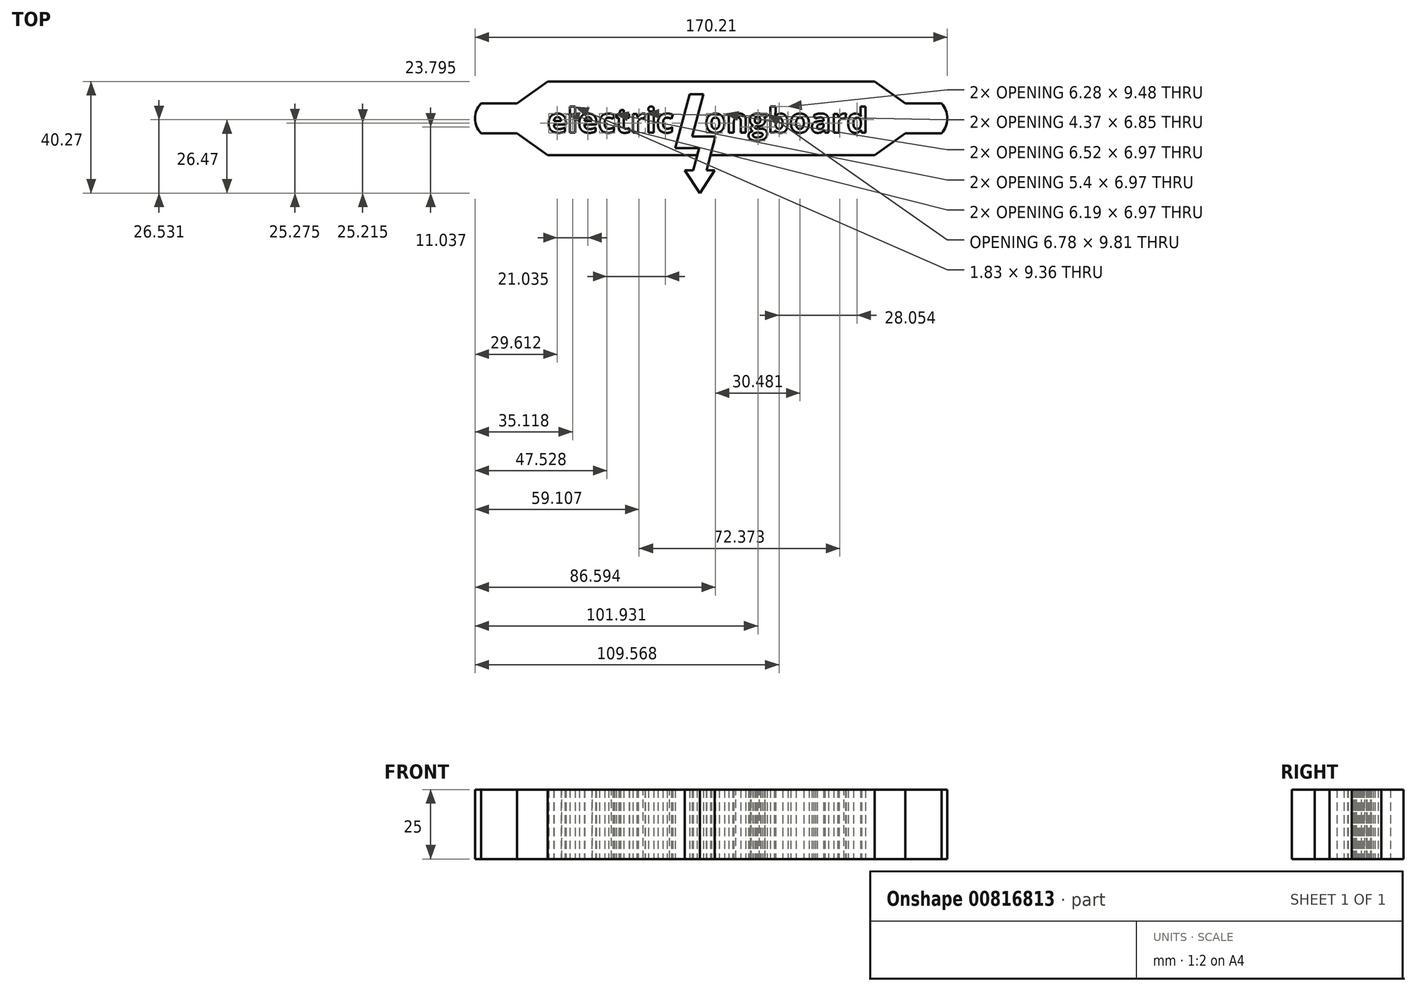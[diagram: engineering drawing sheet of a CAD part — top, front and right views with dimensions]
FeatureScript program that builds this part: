
annotation { "Feature Type Name" : "Feature", "Feature Type Description" : "" }
export const myFeature = defineFeature(function(context is Context, id is Id, definition is map)
    precondition{}
    {
        {
            var Q0;
            Q0=qCreatedBy(makeId("Top.planeOp"),FACE);
            var sketch = newSketch(context, id + "F0", { "sketchPlane" : qUnion([Q0])});
            skText(sketch, "E0", { "text": "electric", "fontName": "OpenSans-Bold.ttf"});
            skLineSegment(sketch, "E1", {"start": v(0.03, 13.79) * mm, "end": v(-5.14, -5.6) * mm});
            skLineSegment(sketch, "E2", {"start": v(-5.14, -5.6) * mm, "end": v(3.45, -5.6) * mm});
            skLineSegment(sketch, "E3", {"start": v(0.03, 13.79) * mm, "end": v(5.04, 13.79) * mm});
            skLineSegment(sketch, "E4", {"start": v(5.04, 13.79) * mm, "end": v(0.98, -1.43) * mm});
            skLineSegment(sketch, "E5", {"start": v(0.98, -1.43) * mm, "end": v(9.37, -1.43) * mm});
            skLineSegment(sketch, "E6", {"start": v(9.37, -1.43) * mm, "end": v(6.13, -13.58) * mm});
            skLineSegment(sketch, "E7", {"start": v(1.32, -13.58) * mm, "end": v(-1.68, -13.58) * mm});
            skLineSegment(sketch, "E8", {"start": v(-1.68, -13.58) * mm, "end": v(3.72, -21.86) * mm});
            skLineSegment(sketch, "E9.MirrorCS", {"start": v(6.12, -13.58) * mm, "end": v(9.12, -13.58) * mm});
            skLineSegment(sketch, "E10.MirrorCS", {"start": v(9.12, -13.58) * mm, "end": v(3.71, -21.86) * mm});
            skText(sketch, "E11", { "text": "ongboard", "fontName": "OpenSans-Bold.ttf"});
            skLineSegment(sketch, "E12", {"start": v(3.45, -5.6) * mm, "end": v(1.32, -13.58) * mm});
            skLineSegment(sketch, "E13", {"start": v(-51.05, 18.42) * mm, "end": v(66.73, 18.42) * mm});
            skLineSegment(sketch, "E14", {"start": v(-51.05, -8.15) * mm, "end": v(2.77, -8.15) * mm});
            skLineSegment(sketch, "E15", {"start": v(-51.05, 18.42) * mm, "end": v(-62.15, 10.5) * mm});
            skLineSegment(sketch, "E16.MirrorCS", {"start": v(-51.05, -8.15) * mm, "end": v(-62.15, -0.22) * mm});
            skLineSegment(sketch, "E17.MirrorCS", {"start": v(66.73, 18.42) * mm, "end": v(77.84, 10.5) * mm});
            skLineSegment(sketch, "E18.MirrorCS", {"start": v(66.73, -8.15) * mm, "end": v(77.84, -0.22) * mm});
            skLineSegment(sketch, "E19", {"start": v(-62.15, 10.5) * mm, "end": v(-75.17, 10.5) * mm});
            skLineSegment(sketch, "E20.MirrorCS", {"start": v(-62.15, -0.22) * mm, "end": v(-75.17, -0.22) * mm});
            skArc(sketch, "E21", {"start": v(-75.17, 10.5) * mm, "mid": v(-77.26, 5.14) * mm, "end": v(-75.17, -0.22) * mm});
            skArc(sketch, "E22.MirrorCS", {"start": v(90.85, 10.5) * mm, "mid": v(92.95, 5.14) * mm, "end": v(90.85, -0.22) * mm});
            skLineSegment(sketch, "E23.MirrorCS", {"start": v(77.84, -0.22) * mm, "end": v(90.85, -0.22) * mm});
            skLineSegment(sketch, "E24.MirrorCS", {"start": v(77.84, 10.5) * mm, "end": v(90.85, 10.5) * mm});
            skLineSegment(sketch, "E25.trimOffspring", {"start": v(7.58, -8.15) * mm, "end": v(66.73, -8.15) * mm});
            const initialGuessF0  = {"E0": [-0.0513, 0, 1, 0, 0.00887], "E11": [0.00552, 0, 1, 0, 0.00887]};
            skSetInitialGuess(sketch, initialGuessF0);
            skSolve(sketch);
        }
        {
            var Q0;
            Q0=makeQuery(id+"F0.imprint","IMPRINT",FACE,{"disambiguationData":[TD([[makeQuery(id+"F0.imprint","IMPRINT",EDGE,{"derivedFrom":sQuery(id+"F0.wireOp",EDGE,"E0.sketch_text.stroke-5")}),1.0]])]});
            extrude(context, id + "F1", {"entities" : qUnion([Q0]), "depth" : 25 * mm, "offsetDistance" : 25 * mm});
        }
        {
            var Q0;
            Q0=makeQuery(id+"F0.imprint","IMPRINT",FACE,{"disambiguationData":[TD([[makeQuery(id+"F0.imprint","IMPRINT",EDGE,{"derivedFrom":sQuery(id+"F0.wireOp",EDGE,"E11.sketch_text.stroke-0")}),1.0]])]});
            var Q1;
            Q1=makeQuery(id+"F0.imprint","IMPRINT",FACE,{"disambiguationData":[TD([[makeQuery(id+"F0.imprint","IMPRINT",EDGE,{"derivedFrom":sQuery(id+"F0.wireOp",EDGE,"E11.sketch_text.stroke-93")}),1.0]])]});
            extrude(context, id + "F2", {"entities" : qUnion([Q0, Q1]), "depth" : 25 * mm, "offsetDistance" : 25 * mm});
        }
        {
            var Q0;
            Q0=makeQuery(id+"F0.imprint","IMPRINT",FACE,{"disambiguationData":[TD([[makeQuery(id+"F0.imprint","IMPRINT",EDGE,{"derivedFrom":sQuery(id+"F0.wireOp",EDGE,"E1")}),1.0]])]});
            extrude(context, id + "F3", {"entities" : qUnion([Q0]), "depth" : 25 * mm, "offsetDistance" : 25 * mm});
        }
        {
            var Q0;
            Q0=makeQuery(id+"F0.imprint","IMPRINT",FACE,{"disambiguationData":[TD([[makeQuery(id+"F0.imprint","IMPRINT",EDGE,{"derivedFrom":sQuery(id+"F0.wireOp",EDGE,"E11.sketch_text.stroke-73")}),1.0]])]});
            var Q1;
            Q1=makeQuery(id+"F0.imprint","IMPRINT",FACE,{"disambiguationData":[TD([[makeQuery(id+"F0.imprint","IMPRINT",EDGE,{"derivedFrom":sQuery(id+"F0.wireOp",EDGE,"E11.sketch_text.stroke-64")}),1.0]])]});
            var Q2;
            Q2=makeQuery(id+"F0.imprint","IMPRINT",FACE,{"disambiguationData":[TD([[makeQuery(id+"F0.imprint","IMPRINT",EDGE,{"derivedFrom":sQuery(id+"F0.wireOp",EDGE,"E11.sketch_text.stroke-102")}),1.0]])]});
            var Q3;
            Q3=makeQuery(id+"F0.imprint","IMPRINT",FACE,{"disambiguationData":[TD([[makeQuery(id+"F0.imprint","IMPRINT",EDGE,{"derivedFrom":sQuery(id+"F0.wireOp",EDGE,"E11.sketch_text.stroke-138")}),1.0]])]});
            var Q4;
            Q4=makeQuery(id+"F0.imprint","IMPRINT",FACE,{"disambiguationData":[TD([[makeQuery(id+"F0.imprint","IMPRINT",EDGE,{"derivedFrom":sQuery(id+"F0.wireOp",EDGE,"E11.sketch_text.stroke-172")}),1.0]])]});
            var Q5;
            Q5=makeQuery(id+"F0.imprint","IMPRINT",FACE,{"disambiguationData":[TD([[makeQuery(id+"F0.imprint","IMPRINT",EDGE,{"derivedFrom":sQuery(id+"F0.wireOp",EDGE,"E0.sketch_text.stroke-0")}),1.0]])]});
            var Q6;
            Q6=makeQuery(id+"F0.imprint","IMPRINT",FACE,{"disambiguationData":[TD([[makeQuery(id+"F0.imprint","IMPRINT",EDGE,{"derivedFrom":sQuery(id+"F0.wireOp",EDGE,"E0.sketch_text.stroke-24")}),1.0]])]});
            extrude(context, id + "F4", {"entities" : qUnion([Q0, Q1, Q2, Q3, Q4, Q5, Q6]), "operationType" : NewBodyOperationType.ADD, "depth" : 25 * mm, "offsetDistance" : 25 * mm});
        }
        {
            var Q0;
            Q0=makeQuery(id+"F0.imprint","IMPRINT",FACE,{"disambiguationData":[TD([[makeQuery(id+"F0.imprint","IMPRINT",EDGE,{"derivedFrom":sQuery(id+"F0.wireOp",EDGE,"E0.sketch_text.stroke-20")}),-1.0]])]});
            var Q1;
            Q1=makeQuery(id+"F0.imprint","IMPRINT",FACE,{"disambiguationData":[TD([[makeQuery(id+"F0.imprint","IMPRINT",EDGE,{"derivedFrom":sQuery(id+"F0.wireOp",EDGE,"E0.sketch_text.stroke-0")}),-1.0]])]});
            var Q2;
            Q2=makeQuery(id+"F0.imprint","IMPRINT",FACE,{"disambiguationData":[TD([[makeQuery(id+"F0.imprint","IMPRINT",EDGE,{"derivedFrom":sQuery(id+"F0.wireOp",EDGE,"E0.sketch_text.stroke-24")}),-1.0]])]});
            var Q3;
            Q3=makeQuery(id+"F0.imprint","IMPRINT",FACE,{"disambiguationData":[TD([[makeQuery(id+"F0.imprint","IMPRINT",EDGE,{"derivedFrom":sQuery(id+"F0.wireOp",EDGE,"E0.sketch_text.stroke-44")}),-1.0]])]});
            var Q4;
            Q4=makeQuery(id+"F0.imprint","IMPRINT",FACE,{"disambiguationData":[TD([[makeQuery(id+"F0.imprint","IMPRINT",EDGE,{"derivedFrom":sQuery(id+"F0.wireOp",EDGE,"E0.sketch_text.stroke-58")}),-1.0]])]});
            var Q5;
            Q5=makeQuery(id+"F0.imprint","IMPRINT",FACE,{"disambiguationData":[TD([[makeQuery(id+"F0.imprint","IMPRINT",EDGE,{"derivedFrom":sQuery(id+"F0.wireOp",EDGE,"E0.sketch_text.stroke-76")}),-1.0]])]});
            var Q6;
            Q6=makeQuery(id+"F0.imprint","IMPRINT",FACE,{"disambiguationData":[TD([[makeQuery(id+"F0.imprint","IMPRINT",EDGE,{"derivedFrom":sQuery(id+"F0.wireOp",EDGE,"E0.sketch_text.stroke-89")}),-1.0]])]});
            var Q7;
            Q7=makeQuery(id+"F0.imprint","IMPRINT",FACE,{"disambiguationData":[TD([[makeQuery(id+"F0.imprint","IMPRINT",EDGE,{"derivedFrom":sQuery(id+"F0.wireOp",EDGE,"E0.sketch_text.stroke-94")}),-1.0]])]});
            var Q8;
            Q8=makeQuery(id+"F0.imprint","IMPRINT",FACE,{"disambiguationData":[TD([[makeQuery(id+"F0.imprint","IMPRINT",EDGE,{"derivedFrom":sQuery(id+"F0.wireOp",EDGE,"E0.sketch_text.stroke-98")}),-1.0]])]});
            var Q9;
            Q9=makeQuery(id+"F0.imprint","IMPRINT",FACE,{"disambiguationData":[TD([[makeQuery(id+"F0.imprint","IMPRINT",EDGE,{"derivedFrom":sQuery(id+"F0.wireOp",EDGE,"E11.sketch_text.stroke-0")}),-1.0]])]});
            var Q10;
            Q10=makeQuery(id+"F0.imprint","IMPRINT",FACE,{"disambiguationData":[TD([[makeQuery(id+"F0.imprint","IMPRINT",EDGE,{"derivedFrom":sQuery(id+"F0.wireOp",EDGE,"E11.sketch_text.stroke-18")}),-1.0]])]});
            var Q11;
            Q11=makeQuery(id+"F0.imprint","IMPRINT",FACE,{"disambiguationData":[TD([[makeQuery(id+"F0.imprint","IMPRINT",EDGE,{"derivedFrom":sQuery(id+"F0.wireOp",EDGE,"E11.sketch_text.stroke-35")}),-1.0]])]});
            var Q12;
            Q12=makeQuery(id+"F0.imprint","IMPRINT",FACE,{"disambiguationData":[TD([[makeQuery(id+"F0.imprint","IMPRINT",EDGE,{"derivedFrom":sQuery(id+"F0.wireOp",EDGE,"E11.sketch_text.stroke-79")}),-1.0]])]});
            var Q13;
            Q13=makeQuery(id+"F0.imprint","IMPRINT",FACE,{"disambiguationData":[TD([[makeQuery(id+"F0.imprint","IMPRINT",EDGE,{"derivedFrom":sQuery(id+"F0.wireOp",EDGE,"E11.sketch_text.stroke-102")}),-1.0]])]});
            var Q14;
            Q14=makeQuery(id+"F0.imprint","IMPRINT",FACE,{"disambiguationData":[TD([[makeQuery(id+"F0.imprint","IMPRINT",EDGE,{"derivedFrom":sQuery(id+"F0.wireOp",EDGE,"E11.sketch_text.stroke-120")}),-1.0]])]});
            var Q15;
            Q15=makeQuery(id+"F0.imprint","IMPRINT",FACE,{"disambiguationData":[TD([[makeQuery(id+"F0.imprint","IMPRINT",EDGE,{"derivedFrom":sQuery(id+"F0.wireOp",EDGE,"E11.sketch_text.stroke-145")}),-1.0]])]});
            var Q16;
            Q16=makeQuery(id+"F0.imprint","IMPRINT",FACE,{"disambiguationData":[TD([[makeQuery(id+"F0.imprint","IMPRINT",EDGE,{"derivedFrom":sQuery(id+"F0.wireOp",EDGE,"E11.sketch_text.stroke-158")}),-1.0]])]});
            extrude(context, id + "F5", {"entities" : qUnion([Q0, Q1, Q2, Q3, Q4, Q5, Q6, Q7, Q8, Q9, Q10, Q11, Q12, Q13, Q14, Q15, Q16]), "depth" : 25 * mm, "offsetDistance" : 25 * mm});
        }
    });
